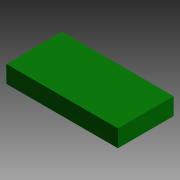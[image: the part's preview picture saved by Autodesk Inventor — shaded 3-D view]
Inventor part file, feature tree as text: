
AUTODESK INVENTOR PART (.ipt)
format: ipt  version: 2013 SP1 (Build 170176100, 176)  size: 82,944 bytes
history: native  units: mm
features: extrude x1, sketch x1
ambient origin geometry x8: Origin, YZ Plane, XZ Plane, XY Plane, X Axis, Y Axis, Z Axis, Center Point
bodies: Volumenkörper1 (feature_tree)
feature tree (2):
  extrude  "Extrusion1"  Depth=65.0mm
  sketch  "Skizze1"  dims[d0=130.0mm d1=65.0mm d2=20.0mm d3=0.0mm]
